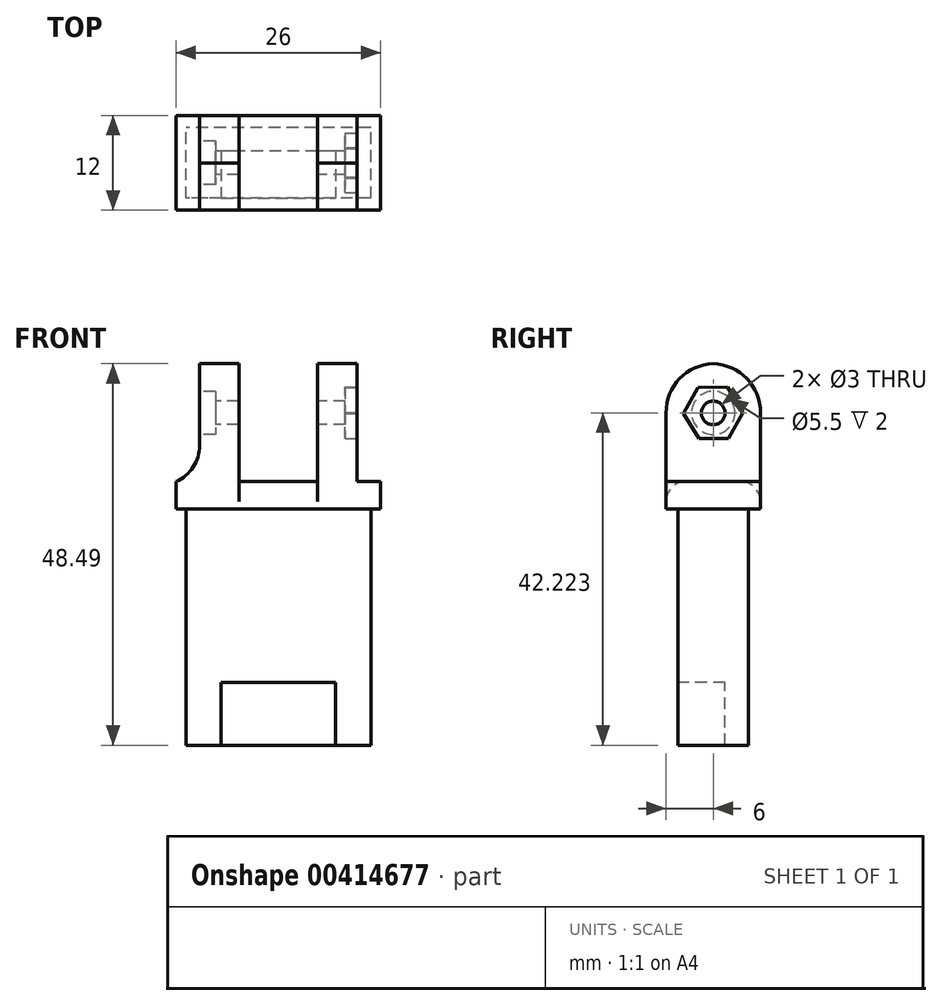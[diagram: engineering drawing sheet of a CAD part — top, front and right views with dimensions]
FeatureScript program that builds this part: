
annotation { "Feature Type Name" : "Feature", "Feature Type Description" : "" }
export const myFeature = defineFeature(function(context is Context, id is Id, definition is map)
    precondition{}
    {
        {
            var Q0;
            Q0=qCreatedBy(makeId("Top.planeOp"),FACE);
            var sketch = newSketch(context, id + "F0", { "sketchPlane" : qUnion([Q0])});
            skLineSegment(sketch, "E0.bottom", {"start": v(11.75, -4.5) * mm, "end": v(-11.75, -4.5) * mm});
            skLineSegment(sketch, "E0.top", {"start": v(11.75, 4.5) * mm, "end": v(-11.75, 4.5) * mm});
            skLineSegment(sketch, "E0.left", {"start": v(11.75, -4.5) * mm, "end": v(11.75, 4.5) * mm});
            skLineSegment(sketch, "E0.right", {"start": v(-11.75, -4.5) * mm, "end": v(-11.75, 4.5) * mm});
            skPoint(sketch, "E0.middle", {"position": v(0, 0) * mm});
            skSolve(sketch);
        }
        {
            var Q0;
            Q0=qCreatedBy(makeId("Top.planeOp"),FACE);
            var sketch = newSketch(context, id + "F1", { "sketchPlane" : qUnion([Q0])});
            skSolve(sketch);
        }
        {
            var Q0;
            Q0 = qSketchRegion(id + "F1", true);
            var Q1;
            Q1=makeQuery(id+"F0.imprint","IMPRINT",FACE,{"disambiguationData":[TD([[makeQuery(id+"F0.imprint","IMPRINT",EDGE,{"derivedFrom":sQuery(id+"F0.wireOp",EDGE,"E0.bottom")}),-1.0]])]});
            extrude(context, id + "F2", {"entities" : qUnion([Q0, Q1]), "oppositeDirection" : true, "depth" : 30 * mm});
        }
        {
            var Q0;
            Q0=makeQuery(id+"F2.opExtrude","CAP_FACE",FACE,{"disambiguationData":[OSD([sQuery(id+"F0.wireOp",EDGE,"E0.bottom"),sQuery(id+"F0.wireOp",EDGE,"E0.top"),sQuery(id+"F0.wireOp",EDGE,"E0.left"),sQuery(id+"F0.wireOp",EDGE,"E0.right")])],"isStart":true});
            var sketch = newSketch(context, id + "F3", { "sketchPlane" : qUnion([Q0])});
            skLineSegment(sketch, "E1.bottom", {"start": v(13, -6) * mm, "end": v(-13, -6) * mm});
            skLineSegment(sketch, "E1.top", {"start": v(13, 6) * mm, "end": v(-13, 6) * mm});
            skLineSegment(sketch, "E1.left", {"start": v(13, -6) * mm, "end": v(13, 6) * mm});
            skLineSegment(sketch, "E1.right", {"start": v(-13, -6) * mm, "end": v(-13, 6) * mm});
            skPoint(sketch, "E1.middle", {"position": v(0, 0) * mm});
            skSolve(sketch);
        }
        {
            var Q0;
            Q0=makeQuery(id+"F3.imprint","IMPRINT",FACE,{"disambiguationData":[TD([[makeQuery(id+"F3.imprint","IMPRINT",EDGE,{"derivedFrom":sQuery(id+"F3.wireOp",EDGE,"E1.bottom")}),-1.0]])]});
            var Q1;
            Q1=makeQuery(id+"F3.imprint","IMPRINT",FACE,{"disambiguationData":[TD([[makeQuery(id+"F3.imprint","IMPRINT",EDGE,{"derivedFrom":makeQuery(id+"F2.opExtrude","CAP_EDGE",EDGE,{"disambiguationData":[OSD([sQuery(id+"F0.wireOp",EDGE,"E0.bottom")])],"isStart":true})}),-1.0]])]});
            extrude(context, id + "F4", {"entities" : qUnion([Q0, Q1]), "depth" : 3.5 * mm});
        }
        {
            var Q0;
            Q0=makeQuery(id+"F4.opExtrude","CAP_FACE",FACE,{"disambiguationData":[OSD([sQuery(id+"F3.wireOp",EDGE,"E1.bottom"),sQuery(id+"F3.wireOp",EDGE,"E1.top"),sQuery(id+"F3.wireOp",EDGE,"E1.left"),sQuery(id+"F3.wireOp",EDGE,"E1.right")])],"isStart":false});
            var sketch = newSketch(context, id + "F5", { "sketchPlane" : qUnion([Q0])});
            skLineSegment(sketch, "E2", {"start": v(0, 6) * mm, "end": v(0, -6) * mm, "construction": true});
            skLineSegment(sketch, "E3", {"start": v(-7.5, 6) * mm, "end": v(-7.5, -6) * mm, "construction": true});
            skLineSegment(sketch, "E4.bottom", {"start": v(-5, -6) * mm, "end": v(-10, -6) * mm});
            skLineSegment(sketch, "E4.top", {"start": v(-5, 6) * mm, "end": v(-10, 6) * mm});
            skLineSegment(sketch, "E4.left", {"start": v(-5, -6) * mm, "end": v(-5, 6) * mm});
            skLineSegment(sketch, "E4.right", {"start": v(-10, -6) * mm, "end": v(-10, 6) * mm});
            skPoint(sketch, "E4.middle", {"position": v(-7.5, 0) * mm});
            skLineSegment(sketch, "E5.MirrorCS", {"start": v(5, -6) * mm, "end": v(5, 6) * mm});
            skLineSegment(sketch, "E6.MirrorCS", {"start": v(5, -6) * mm, "end": v(10, -6) * mm});
            skLineSegment(sketch, "E7.MirrorCS", {"start": v(10, -6) * mm, "end": v(10, 6) * mm});
            skLineSegment(sketch, "E8.MirrorCS", {"start": v(5, 6) * mm, "end": v(10, 6) * mm});
            skSolve(sketch);
        }
        {
            var Q0;
            {var subQ0=sQuery(id+"F5.wireOp",EDGE,"E4.right");Q0=makeQuery(id+"F5.imprint","IMPRINT",FACE,{"disambiguationData":[TD([[makeQuery(id+"F5.imprint","IMPRINT",EDGE,{"derivedFrom":subQ0}),1.0]])]});}
            var sketch = newSketch(context, id + "F6", { "sketchPlane" : qUnion([Q0])});
            skSolve(sketch);
        }
        {
            var Q0;
            Q0 = qSketchRegion(id + "F6", true);
            var Q1;
            Q1=makeQuery(id+"F5.imprint","IMPRINT",FACE,{"disambiguationData":[TD([[makeQuery(id+"F5.imprint","IMPRINT",EDGE,{"derivedFrom":sQuery(id+"F5.wireOp",EDGE,"E4.bottom")}),-1.0]])]});
            var Q2;
            Q2=makeQuery(id+"F5.imprint","IMPRINT",FACE,{"disambiguationData":[TD([[makeQuery(id+"F5.imprint","IMPRINT",EDGE,{"derivedFrom":sQuery(id+"F5.wireOp",EDGE,"E5.MirrorCS")}),-1.0]])]});
            extrude(context, id + "F7", {"entities" : qUnion([Q0, Q1, Q2]), "operationType" : NewBodyOperationType.ADD, "depth" : 15 * mm});
        }
        {
            var Q0;
            Q0=makeQuery(id+"F7.opExtrude","CAP_EDGE",EDGE,{"disambiguationData":[OSD([sQuery(id+"F5.wireOp",EDGE,"E4.bottom")])],"isStart":false});
            var Q1;
            Q1=makeQuery(id+"F7.opExtrude","CAP_EDGE",EDGE,{"disambiguationData":[OSD([sQuery(id+"F5.wireOp",EDGE,"E4.top")])],"isStart":false});
            var Q2;
            Q2=makeQuery(id+"F7.opExtrude","CAP_EDGE",EDGE,{"disambiguationData":[OSD([sQuery(id+"F5.wireOp",EDGE,"E8.MirrorCS")])],"isStart":false});
            var Q3;
            Q3=makeQuery(id+"F7.opExtrude","CAP_EDGE",EDGE,{"disambiguationData":[OSD([sQuery(id+"F5.wireOp",EDGE,"E6.MirrorCS")])],"isStart":false});
            fillet(context, id + "F8", {"entities" : qUnion([Q0, Q1, Q2, Q3]), "radius" : 6.28 * mm, "tangentPropagation" : true, "allowEdgeOverflow" : false});
        }
        {
            var Q0;
            Q0=makeQuery(id+"F7.opExtrude","SWEPT_FACE",FACE,{"disambiguationData":[OSD([sQuery(id+"F5.wireOp",EDGE,"E4.right")])]});
            var sketch = newSketch(context, id + "F9", { "sketchPlane" : qUnion([Q0])});
            skLineSegment(sketch, "E9", {"start": v(0, 3.5) * mm, "end": v(0, 18.5) * mm, "construction": true});
            skLineSegment(sketch, "E10", {"start": v(-6, 12.22) * mm, "end": v(6, 12.22) * mm, "construction": true});
            skCircle(sketch, "E11", {"center": v(0, 12.22) * mm, "radius": 1.5 * mm});
            skCircle(sketch, "E12", {"center": v(0, 12.22) * mm, "radius": 2.75 * mm});
            skSolve(sketch);
        }
        {
            var Q0;
            Q0=makeQuery(id+"F7.opExtrude","SWEPT_FACE",FACE,{"disambiguationData":[OSD([sQuery(id+"F5.wireOp",EDGE,"E7.MirrorCS")])]});
            var sketch = newSketch(context, id + "F10", { "sketchPlane" : qUnion([Q0])});
            skLineSegment(sketch, "E13", {"start": v(6, 12.22) * mm, "end": v(-6, 12.22) * mm, "construction": true});
            skLineSegment(sketch, "E14", {"start": v(0, 18.5) * mm, "end": v(0, 12.22) * mm, "construction": true});
            skCircle(sketch, "E15.cCircle", {"center": v(0, 12.22) * mm, "radius": 3.25 * mm, "construction": true});
            skLineSegment(sketch, "E15.0", {"start": v(3.75, 12.28) * mm, "end": v(1.92, 9) * mm});
            skLineSegment(sketch, "E15.1", {"start": v(1.92, 9) * mm, "end": v(-1.83, 8.95) * mm});
            skLineSegment(sketch, "E15.2", {"start": v(-1.83, 8.95) * mm, "end": v(-3.75, 12.17) * mm});
            skLineSegment(sketch, "E15.3", {"start": v(-3.75, 12.17) * mm, "end": v(-1.92, 15.45) * mm});
            skLineSegment(sketch, "E15.4", {"start": v(-1.92, 15.45) * mm, "end": v(1.83, 15.5) * mm});
            skLineSegment(sketch, "E15.5", {"start": v(1.83, 15.5) * mm, "end": v(3.75, 12.28) * mm});
            skPoint(sketch, "E15.0.midPoint", {"position": v(2.84, 10.64) * mm});
            skSolve(sketch);
        }
        {
            var Q0;
            Q0=makeQuery(id+"F10.imprint","IMPRINT",FACE,{"disambiguationData":[TD([[makeQuery(id+"F10.imprint","IMPRINT",EDGE,{"derivedFrom":sQuery(id+"F10.wireOp",EDGE,"E15.0")}),1.0]])]});
            var sketch = newSketch(context, id + "F11", { "sketchPlane" : qUnion([Q0])});
            skSolve(sketch);
        }
        {
            var Q0;
            Q0 = qSketchRegion(id + "F11", true);
            var Q1;
            Q1=makeQuery(id+"F10.imprint","IMPRINT",FACE,{"disambiguationData":[TD([[makeQuery(id+"F10.imprint","IMPRINT",EDGE,{"derivedFrom":sQuery(id+"F10.wireOp",EDGE,"E15.0")}),-1.0]])]});
            extrude(context, id + "F12", {"entities" : qUnion([Q0, Q1]), "operationType" : NewBodyOperationType.REMOVE, "oppositeDirection" : true, "depth" : 1.5 * mm});
        }
        {
            var Q0;
            Q0=makeQuery(id+"F9.imprint","IMPRINT",FACE,{"disambiguationData":[TD([[makeQuery(id+"F9.imprint","IMPRINT",EDGE,{"derivedFrom":sQuery(id+"F9.wireOp",EDGE,"E11")}),-1.0]])]});
            var sketch = newSketch(context, id + "F13", { "sketchPlane" : qUnion([Q0])});
            skSolve(sketch);
        }
        {
            var Q0;
            Q0 = qSketchRegion(id + "F13", true);
            var Q1;
            Q1=makeQuery(id+"F9.imprint","IMPRINT",FACE,{"disambiguationData":[TD([[makeQuery(id+"F9.imprint","IMPRINT",EDGE,{"derivedFrom":sQuery(id+"F9.wireOp",EDGE,"E11")}),1.0]])]});
            extrude(context, id + "F14", {"entities" : qUnion([Q0, Q1]), "operationType" : NewBodyOperationType.REMOVE, "oppositeDirection" : true, "depth" : 25 * mm});
        }
        {
            var Q0;
            Q0=makeQuery(id+"F2.opExtrude","SWEPT_FACE",FACE,{"disambiguationData":[OSD([sQuery(id+"F0.wireOp",EDGE,"E0.bottom")])]});
            var sketch = newSketch(context, id + "F15", { "sketchPlane" : qUnion([Q0])});
            skLineSegment(sketch, "E16", {"start": v(0, -30) * mm, "end": v(0, 0) * mm, "construction": true});
            skLineSegment(sketch, "E17.bottom", {"start": v(0, -30) * mm, "end": v(7.25, -30) * mm});
            skLineSegment(sketch, "E17.top", {"start": v(0, -22) * mm, "end": v(7.25, -22) * mm});
            skLineSegment(sketch, "E17.left", {"start": v(0, -30) * mm, "end": v(0, -22) * mm});
            skLineSegment(sketch, "E17.right", {"start": v(7.25, -30) * mm, "end": v(7.25, -22) * mm});
            skLineSegment(sketch, "E18.MirrorCS", {"start": v(0, -22) * mm, "end": v(-7.25, -22) * mm});
            skLineSegment(sketch, "E19.MirrorCS", {"start": v(-7.25, -30) * mm, "end": v(-7.25, -22) * mm});
            skLineSegment(sketch, "E20.MirrorCS", {"start": v(0, -30) * mm, "end": v(-7.25, -30) * mm});
            skSolve(sketch);
        }
        {
            var Q0;
            Q0=makeQuery(id+"F15.imprint","IMPRINT",FACE,{"disambiguationData":[TD([[makeQuery(id+"F15.imprint","IMPRINT",EDGE,{"derivedFrom":sQuery(id+"F15.wireOp",EDGE,"E17.top")}),1.0]])]});
            var sketch = newSketch(context, id + "F16", { "sketchPlane" : qUnion([Q0])});
            skSolve(sketch);
        }
        {
            var Q0;
            Q0 = qSketchRegion(id + "F16", true);
            var Q1;
            Q1=makeQuery(id+"F15.imprint","IMPRINT",FACE,{"disambiguationData":[TD([[makeQuery(id+"F15.imprint","IMPRINT",EDGE,{"derivedFrom":sQuery(id+"F15.wireOp",EDGE,"E17.bottom")}),-1.0]])]});
            var Q2;
            Q2=makeQuery(id+"F15.imprint","IMPRINT",FACE,{"disambiguationData":[TD([[makeQuery(id+"F15.imprint","IMPRINT",EDGE,{"derivedFrom":sQuery(id+"F15.wireOp",EDGE,"E17.left")}),1.0]])]});
            extrude(context, id + "F17", {"entities" : qUnion([Q0, Q1, Q2]), "operationType" : NewBodyOperationType.REMOVE, "oppositeDirection" : true, "depth" : 6 * mm});
        }
        {
            var Q0;
            Q0=makeQuery(id+"F7.opExtrude","CAP_EDGE",EDGE,{"disambiguationData":[OSD([sQuery(id+"F5.wireOp",EDGE,"E7.MirrorCS")])],"isStart":true});
            var Q1;
            Q1=makeQuery(id+"F7.opExtrude","CAP_EDGE",EDGE,{"disambiguationData":[OSD([sQuery(id+"F5.wireOp",EDGE,"E4.right")])],"isStart":true});
            fillet(context, id + "F18", {"entities" : qUnion([Q0, Q1]), "radius" : 5 * mm, "tangentPropagation" : true, "allowEdgeOverflow" : false});
        }
        {
            var Q0;
            {var subQ0=sQuery(id+"F3.wireOp",EDGE,"E1.top");Q0=makeQuery(id+"F7.boolean.opBoolean","SPLIT",EDGE,{"disambiguationData":[TD([makeQuery(id+"F7.opExtrude","SWEPT_FACE",FACE,{"disambiguationData":[OSD([sQuery(id+"F5.wireOp",EDGE,"E4.left")])]})])],"derivedFrom":makeQuery(id+"F4.opExtrude","CAP_EDGE",EDGE,{"disambiguationData":[OSD([subQ0])],"isStart":false})});}
            var Q1;
            {var subQ0=sQuery(id+"F3.wireOp",EDGE,"E1.bottom");Q1=makeQuery(id+"F7.boolean.opBoolean","SPLIT",EDGE,{"disambiguationData":[TD([makeQuery(id+"F7.opExtrude","SWEPT_FACE",FACE,{"disambiguationData":[OSD([sQuery(id+"F5.wireOp",EDGE,"E4.left")])]})])],"derivedFrom":makeQuery(id+"F4.opExtrude","CAP_EDGE",EDGE,{"disambiguationData":[OSD([subQ0])],"isStart":false})});}
            fillet(context, id + "F19", {"entities" : qUnion([Q0, Q1]), "radius" : 2.5 * mm, "tangentPropagation" : true, "allowEdgeOverflow" : false});
        }
        {
            var Q0;
            Q0=makeQuery(id+"F9.imprint","IMPRINT",FACE,{"disambiguationData":[TD([[makeQuery(id+"F9.imprint","IMPRINT",EDGE,{"derivedFrom":sQuery(id+"F9.wireOp",EDGE,"E11")}),-1.0]])]});
            extrude(context, id + "F20", {"entities" : qUnion([Q0]), "operationType" : NewBodyOperationType.REMOVE, "oppositeDirection" : true, "depth" : 2 * mm});
        }
    });
